# Revit family: EU_EHS_ODU_UB3
name_source: partatom
category: Mechanical Equipment
revit_build: Autodesk Revit 2015 (Build: 20140606_1530(x64)
units: mm (PartAtom-declared; Revit-internal decimal feet)

## types (16) — shared parameters
Designation = -
Fan Grill Depth = 750.00 mm
Fan Grill Height = 36.00 mm
Fan Grill Radius = 375.00 mm
Fan Grill Width = 750.00 mm
Free Content Downloads = -
Location = -
Manufacturer = SAMSUNG
Manufacturer Metadata = -
Notes = -
Product Documentation Link = -
Product Page URL = -
Refrigerant Type = R410A
Sales Rep Locator = -
Subscribe for Update Alerts = -
System Served = -
URL = www.samsung.com

## per-type parameters (varying)
| type | Model | Net Weight | Serial Number |
| 12.00 kW, 220-240V, HEAT PUMP, SPLIT | AE120JXEDEH/EU | 100.00 kg | - |
| 14.00 kW, 220-240V, HEAT PUMP, SPLIT | AE140JXEDEH/EU | 100.00 kg | - |
| 16.00 kW, 220-240V, HEAT PUMP, SPLIT | AE160JXEDEH/EU | 100.00 kg | - |
| 12.00 kW, 380-415V, HEAT PUMP, SPLIT | AE120JXEDGH/EU | 101.50 kg | - |
| 14.00 kW, 380-415V, HEAT PUMP, SPLIT | AE140JXEDGH/EU | 101.50 kg | - |
| 16.00 kW, 380-415V, HEAT PUMP, SPLIT | AE160JXEDGH/EU | 101.50 kg | - |
| 12.00 kW, 220-240V, HEAT PUMP, MONO | AE120JXYDEH/EU | 108.00 kg | - |
| 14.00 kW, 220-240V, HEAT PUMP, MONO | AE140JXYDEH/EU | 108.00 kg |  |
| 16.00 kW, 220-240V, HEAT PUMP, MONO | AE160JXYDEH/EU | 108.00 kg |  |
| 12.00 kW, 380-415V, HEAT PUMP, MONO | AE120JXYDGH/EU | 108.00 kg | - |
| 14.00 kW, 380-415V, HEAT PUMP, MONO | AE140JXYDGH/EU | 108.00 kg |  |
| 16.00 kW, 380-415V, HEAT PUMP, MONO | AE160JXYDGH/EU | 108.00 kg |  |
| 12.00 kW, 220-240V, HEAT PUMP, TDM PLUS | AE120MXTPEH/EU | 107.00 kg | - |
| 16.00 kW, 220-240V, HEAT PUMP, TDM PLUS | AE160MXTPEH/EU | 107.00 kg | - |
| 12.00 kW, 380-415V, HEAT PUMP, TDM PLUS | AE120MXTPGH/EU | 107.00 kg | - |
| 16.00 kW, 380-415V, HEAT PUMP, TDM PLUS | AE160MXTPGH/EU | 107.00 kg | - |

## geometry (parser evidence)
native form markers: Sweep x28
no freeform markers — native parametric forms only
